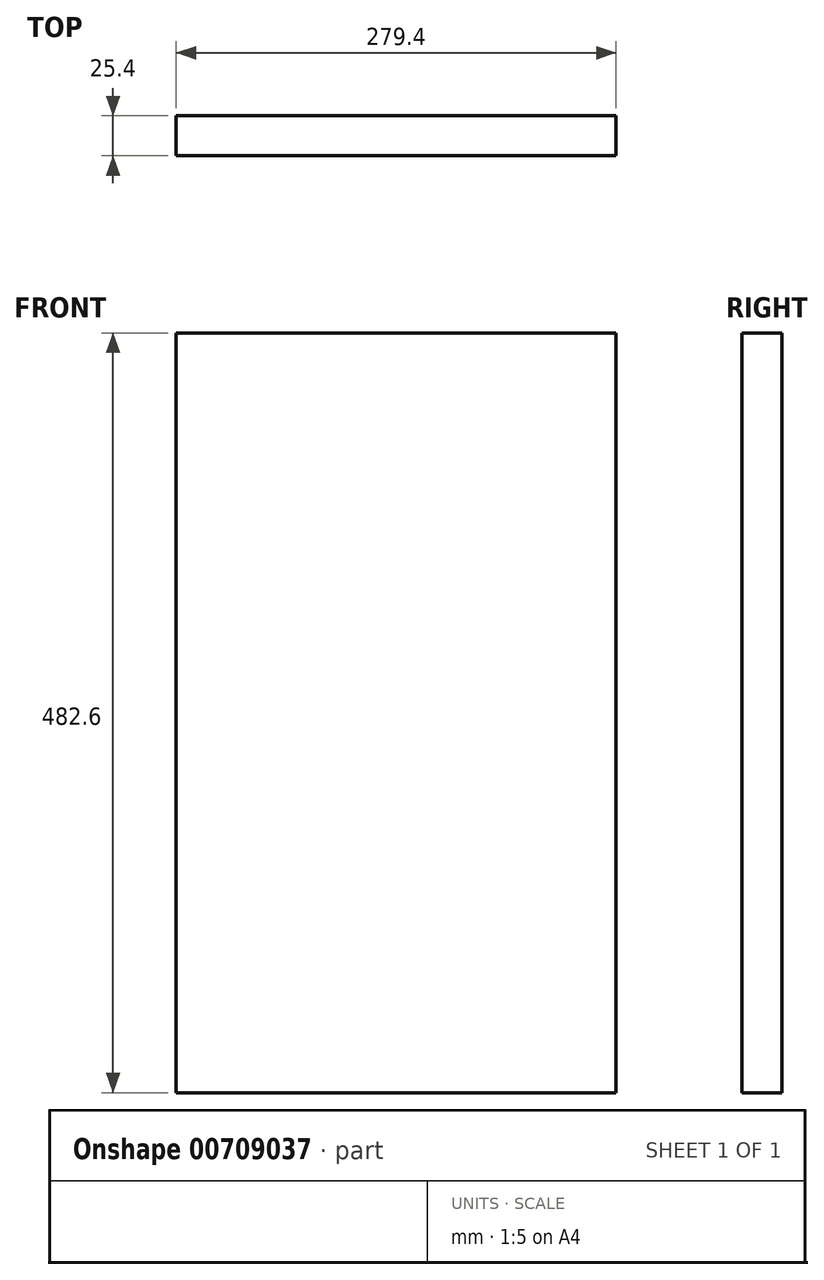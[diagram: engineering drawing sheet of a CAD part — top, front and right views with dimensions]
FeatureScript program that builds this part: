
annotation { "Feature Type Name" : "Feature", "Feature Type Description" : "" }
export const myFeature = defineFeature(function(context is Context, id is Id, definition is map)
    precondition{}
    {
        {
            var Q0;
            Q0=qCreatedBy(makeId("Front.planeOp"),FACE);
            var sketch = newSketch(context, id + "F0", { "sketchPlane" : qUnion([Q0])});
            skLineSegment(sketch, "E0.bottom", {"start": v(117.65, -223.63) * mm, "end": v(-161.75, -223.63) * mm});
            skLineSegment(sketch, "E0.top", {"start": v(117.65, 258.97) * mm, "end": v(-161.75, 258.97) * mm});
            skLineSegment(sketch, "E0.left", {"start": v(117.65, -223.63) * mm, "end": v(117.65, 258.97) * mm});
            skLineSegment(sketch, "E0.right", {"start": v(-161.75, -223.63) * mm, "end": v(-161.75, 258.97) * mm});
            skSolve(sketch);
        }
        {
            var Q0;
            Q0 = qSketchRegion(id + "F0", true);
            extrude(context, id + "F1", {"entities" : qUnion([Q0]), "depth" : 25.4 * mm, "offsetDistance" : 25.4 * mm});
        }
    });
